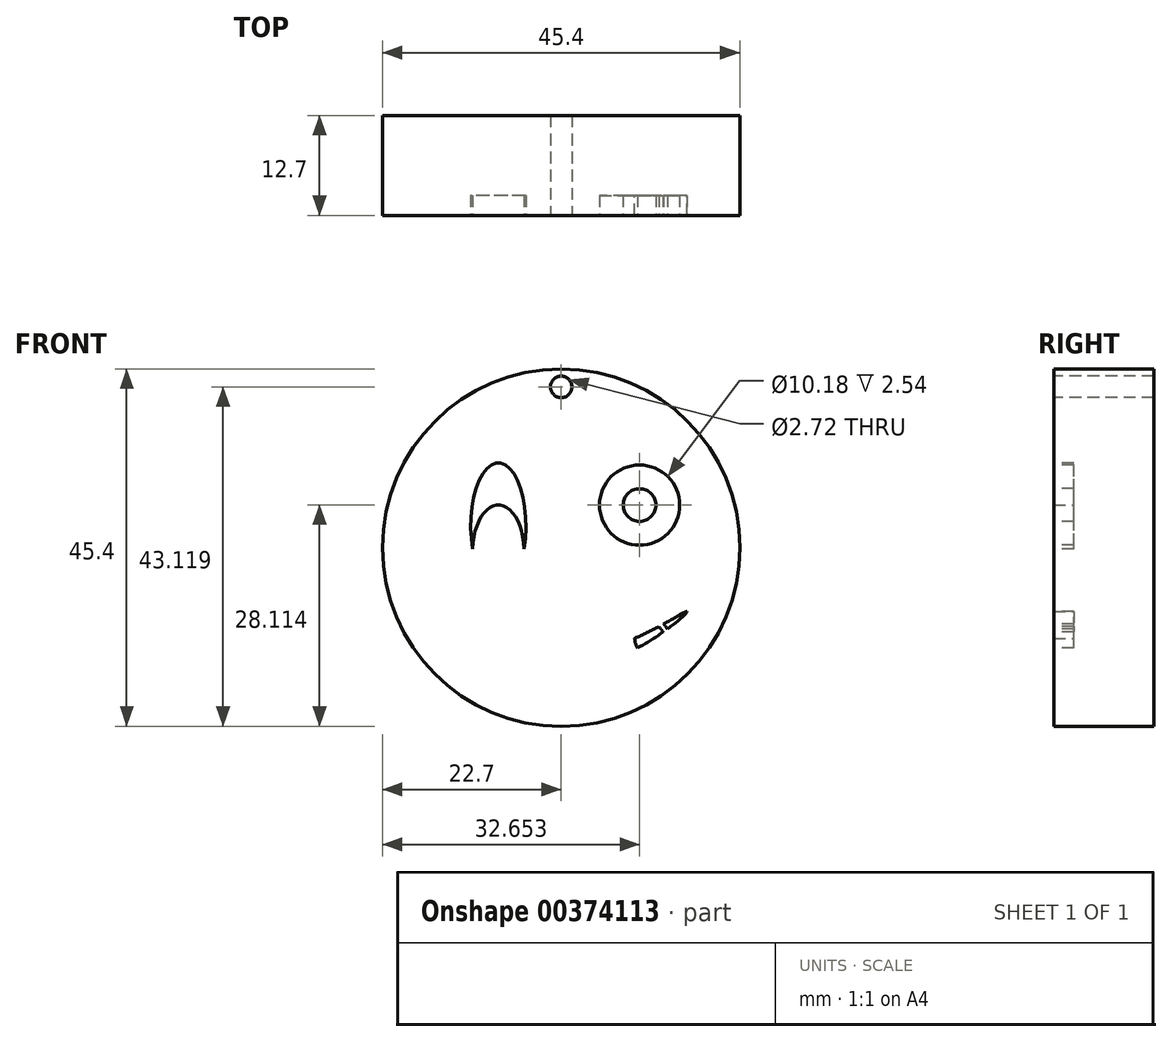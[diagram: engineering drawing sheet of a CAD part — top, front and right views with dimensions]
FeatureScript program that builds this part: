
annotation { "Feature Type Name" : "Feature", "Feature Type Description" : "" }
export const myFeature = defineFeature(function(context is Context, id is Id, definition is map)
    precondition{}
    {
        {
            var Q0;
            Q0=qCreatedBy(makeId("Front.planeOp"),FACE);
            var sketch = newSketch(context, id + "F0", { "sketchPlane" : qUnion([Q0])});
            skCircle(sketch, "E0", {"center": v(0, 0) * mm, "radius": 22.7 * mm});
            skSolve(sketch);
        }
        {
            var Q0;
            Q0=makeQuery(id+"F0.imprint","IMPRINT",FACE,{"disambiguationData":[TD([[makeQuery(id+"F0.imprint","IMPRINT",EDGE,{"derivedFrom":sQuery(id+"F0.wireOp",EDGE,"E0")}),1.0]])]});
            extrude(context, id + "F1", {"entities" : qUnion([Q0]), "depth" : 12.7 * mm});
        }
        {
            var Q0;
            Q0=makeQuery(id+"F1.opExtrude","CAP_FACE",FACE,{"disambiguationData":[OSD([sQuery(id+"F0.wireOp",EDGE,"E0")])],"isStart":false});
            var sketch = newSketch(context, id + "F2", { "sketchPlane" : qUnion([Q0])});
            skEllipticalArc(sketch, "E1", {});
            skEllipticalArc(sketch, "E2", {});
            skFitSpline(sketch, "E3", {"points": [v(-16.1, -8.29) * mm, v(-0.36, -15.68) * mm, v(16, -8.1) * mm, v(-0.36, -13.88) * mm, v(-16.1, -8.29) * mm]});
            skFitSpline(sketch, "E4", {"points": [v(16, -8.1) * mm, v(16.49, -15.6) * mm, v(9.33, -11.53) * mm, v(16, -8.1) * mm]});
            skEllipticalArc(sketch, "E5", {});
            skCircle(sketch, "E6", {"center": v(9.95, 5.41) * mm, "radius": 5.09 * mm});
            skCircle(sketch, "E7", {"center": v(9.95, 5.41) * mm, "radius": 2.08 * mm});
            const initialGuessF2  = {"E1": [-0.00798518002748612, 0.002836274944016495, 0, 1, 0.007933032233268023, 0.003504754738852713, 4.327223935529677, 1.9559613716499085], "E2": [-0.00798518002748612, -0.0003820978740660761, 0, -1, 0.005796437151730061, 0.003250721503016386, 1.6118393743180706, 4.671345932861516], "E5": [0.012722297295366452, -0.009857580734337448, 0.5978106483397688, -0.8016373424009047, 0.004234819493438222, 0.0003414077873771633, 4.700394494684409, 1.5593019218451307]};
            skSetInitialGuess(sketch, initialGuessF2);
            skSolve(sketch);
        }
        {
            var Q0;
            {var subQ0=sQuery(id+"F2.wireOp",EDGE,"E4");var subQ1=sQuery(id+"F2.wireOp",EDGE,"E3");var subQ2=makeQuery(id+"F2.imprint","INTERSECT",VERTEX,{"disambiguationData":[OD(0.0)],"derivedFrom":[subQ1,subQ0]});Q0=makeQuery(id+"F2.imprint","IMPRINT",FACE,{"disambiguationData":[TD([[makeQuery(id+"F2.imprint","IMPRINT",EDGE,{"disambiguationData":[TD([[subQ2,-1.0]])],"derivedFrom":subQ1}),1.0]])]});}
            var Q1;
            {var subQ0=sQuery(id+"F2.wireOp",EDGE,"E4");var subQ1=sQuery(id+"F2.wireOp",EDGE,"E3");var subQ2=makeQuery(id+"F2.imprint","INTERSECT",VERTEX,{"disambiguationData":[OD(1.0)],"derivedFrom":[subQ1,subQ0]});Q1=makeQuery(id+"F2.imprint","IMPRINT",FACE,{"disambiguationData":[TD([[makeQuery(id+"F2.imprint","IMPRINT",EDGE,{"disambiguationData":[TD([[subQ2,1.0]])],"derivedFrom":subQ1}),1.0]])]});}
            var Q2;
            Q2=makeQuery(id+"F2.imprint","IMPRINT",FACE,{"disambiguationData":[TD([[makeQuery(id+"F2.imprint","IMPRINT",EDGE,{"derivedFrom":sQuery(id+"F2.wireOp",EDGE,"E1")}),1.0]])]});
            var Q3;
            Q3=makeQuery(id+"F2.imprint","IMPRINT",FACE,{"disambiguationData":[TD([[makeQuery(id+"F2.imprint","IMPRINT",EDGE,{"derivedFrom":sQuery(id+"F2.wireOp",EDGE,"b2cc0855-5126-4c04-8e4c-6287035dc418")}),1.0]])]});
            var Q4;
            {var subQ7=sQuery(id+"F2.wireOp",EDGE,"E5");Q4=makeQuery(id+"F2.imprint","IMPRINT",FACE,{"disambiguationData":[TD([[makeQuery(id+"F2.imprint","IMPRINT",EDGE,{"derivedFrom":subQ7}),-1.0]])]});}
            var Q5;
            Q5=makeQuery(id+"F2.imprint","IMPRINT",FACE,{"disambiguationData":[TD([[makeQuery(id+"F2.imprint","IMPRINT",EDGE,{"derivedFrom":sQuery(id+"F2.wireOp",EDGE,"E6")}),1.0]])]});
            extrude(context, id + "F3", {"entities" : qUnion([Q0, Q1, Q2, Q3, Q4, Q5]), "operationType" : NewBodyOperationType.REMOVE, "oppositeDirection" : true, "depth" : 2.54 * mm});
        }
        {
            var Q0;
            Q0=makeQuery(id+"F1.opExtrude","CAP_FACE",FACE,{"disambiguationData":[OSD([sQuery(id+"F0.wireOp",EDGE,"E0")])],"isStart":false});
            var sketch = newSketch(context, id + "F4", { "sketchPlane" : qUnion([Q0])});
            skCircle(sketch, "E8", {"center": v(0, 20.42) * mm, "radius": 1.36 * mm});
            skSolve(sketch);
        }
        {
            var Q0;
            Q0=makeQuery(id+"F4.imprint","IMPRINT",FACE,{"disambiguationData":[TD([[makeQuery(id+"F4.imprint","IMPRINT",EDGE,{"derivedFrom":sQuery(id+"F4.wireOp",EDGE,"E8")}),1.0]])]});
            extrude(context, id + "F5", {"entities" : qUnion([Q0]), "operationType" : NewBodyOperationType.REMOVE, "oppositeDirection" : true, "depth" : 12.7 * mm});
        }
    });
